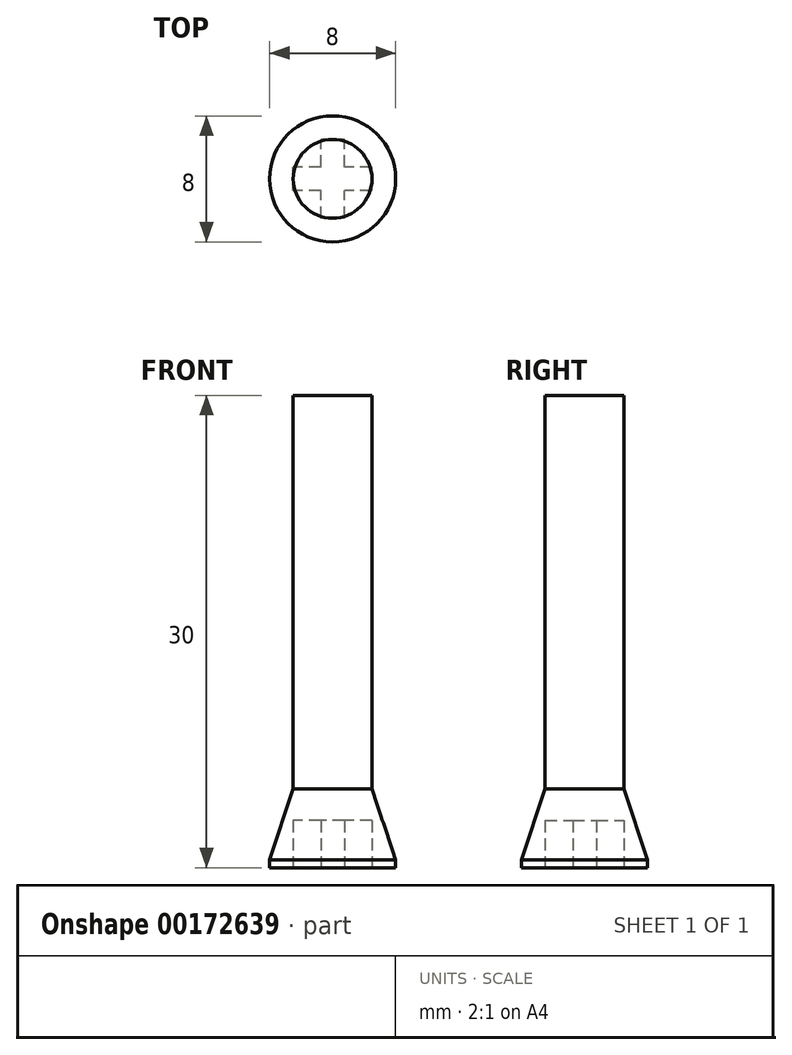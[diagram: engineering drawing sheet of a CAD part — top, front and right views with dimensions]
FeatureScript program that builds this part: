
annotation { "Feature Type Name" : "Feature", "Feature Type Description" : "" }
export const myFeature = defineFeature(function(context is Context, id is Id, definition is map)
    precondition{}
    {
        {
            var Q0;
            Q0=qCreatedBy(makeId("Top.planeOp"),FACE);
            var sketch = newSketch(context, id + "F0", { "sketchPlane" : qUnion([Q0])});
            skCircle(sketch, "E0", {"center": v(0, 0) * mm, "radius": 4 * mm});
            skSolve(sketch);
        }
        {
            var Q0;
            Q0 = qSketchRegion(id + "F0", true);
            extrude(context, id + "F1", {"entities" : qUnion([Q0]), "depth" : 5 * mm});
        }
        {
            var Q0;
            Q0=makeQuery(id+"F1.opExtrude","CAP_FACE",FACE,{"disambiguationData":[OSD([sQuery(id+"F0.wireOp",EDGE,"E0")])],"isStart":false});
            var sketch = newSketch(context, id + "F2", { "sketchPlane" : qUnion([Q0])});
            skCircle(sketch, "E1", {"center": v(0, 0) * mm, "radius": 2.5 * mm});
            skSolve(sketch);
        }
        {
            var Q0;
            Q0 = qSketchRegion(id + "F2", true);
            extrude(context, id + "F3", {"entities" : qUnion([Q0]), "operationType" : NewBodyOperationType.ADD, "depth" : 25 * mm});
        }
        {
            var Q0;
            Q0=qCreatedBy(makeId("Front.planeOp"),FACE);
            var sketch = newSketch(context, id + "F4", { "sketchPlane" : qUnion([Q0])});
            skPoint(sketch, "E2", {"position": v(0, 5) * mm});
            skPoint(sketch, "E3", {"position": v(-4, 5) * mm});
            skPoint(sketch, "E4", {"position": v(-4, 0) * mm});
            skPoint(sketch, "E5", {"position": v(-4, 0.5) * mm});
            skPoint(sketch, "E6", {"position": v(-2.5, 5) * mm});
            skLineSegment(sketch, "E7", {"start": v(-2.5, 5) * mm, "end": v(-4, 0.5) * mm});
            skLineSegment(sketch, "E8", {"start": v(-4, 0.5) * mm, "end": v(-4, 5) * mm});
            skLineSegment(sketch, "E9", {"start": v(-2.5, 5) * mm, "end": v(-4, 5) * mm});
            skLineSegment(sketch, "E10", {"start": v(0, 5) * mm, "end": v(0, 0) * mm});
            skSolve(sketch);
        }
        {
            var Q0;
            Q0 = qSketchRegion(id + "F4", true);
            var Q1;
            Q1=sQuery(id+"F4.wireOp",EDGE,"E10");
            revolve(context, id + "F5", {"operationType" : NewBodyOperationType.REMOVE, "entities" : qUnion([Q0]), "axis" : qUnion([Q1]), "revolveType" : RevolveType.FULL});
        }
        {
            var Q0;
            Q0=makeQuery(id+"F1.opExtrude","CAP_FACE",FACE,{"disambiguationData":[OSD([sQuery(id+"F0.wireOp",EDGE,"E0")])],"isStart":true});
            var sketch = newSketch(context, id + "F6", { "sketchPlane" : qUnion([Q0])});
            skLineSegment(sketch, "E11.bottom", {"start": v(2.5, 0.75) * mm, "end": v(-2.5, 0.75) * mm});
            skLineSegment(sketch, "E11.top", {"start": v(2.5, -0.75) * mm, "end": v(-2.5, -0.75) * mm});
            skLineSegment(sketch, "E11.left", {"start": v(2.5, 0.75) * mm, "end": v(2.5, -0.75) * mm});
            skLineSegment(sketch, "E11.right", {"start": v(-2.5, 0.75) * mm, "end": v(-2.5, -0.75) * mm});
            skPoint(sketch, "E11.middle", {"position": v(0, 0) * mm});
            skLineSegment(sketch, "E12.bottom", {"start": v(0.75, 2.5) * mm, "end": v(-0.75, 2.5) * mm});
            skLineSegment(sketch, "E12.top", {"start": v(0.75, -2.5) * mm, "end": v(-0.75, -2.5) * mm});
            skLineSegment(sketch, "E12.left", {"start": v(0.75, 2.5) * mm, "end": v(0.75, -2.5) * mm});
            skLineSegment(sketch, "E12.right", {"start": v(-0.75, 2.5) * mm, "end": v(-0.75, -2.5) * mm});
            skSolve(sketch);
        }
        {
            var Q0;
            Q0 = qSketchRegion(id + "F6", true);
            extrude(context, id + "F7", {"entities" : qUnion([Q0]), "operationType" : NewBodyOperationType.REMOVE, "oppositeDirection" : true, "depth" : 3 * mm});
        }
    });
